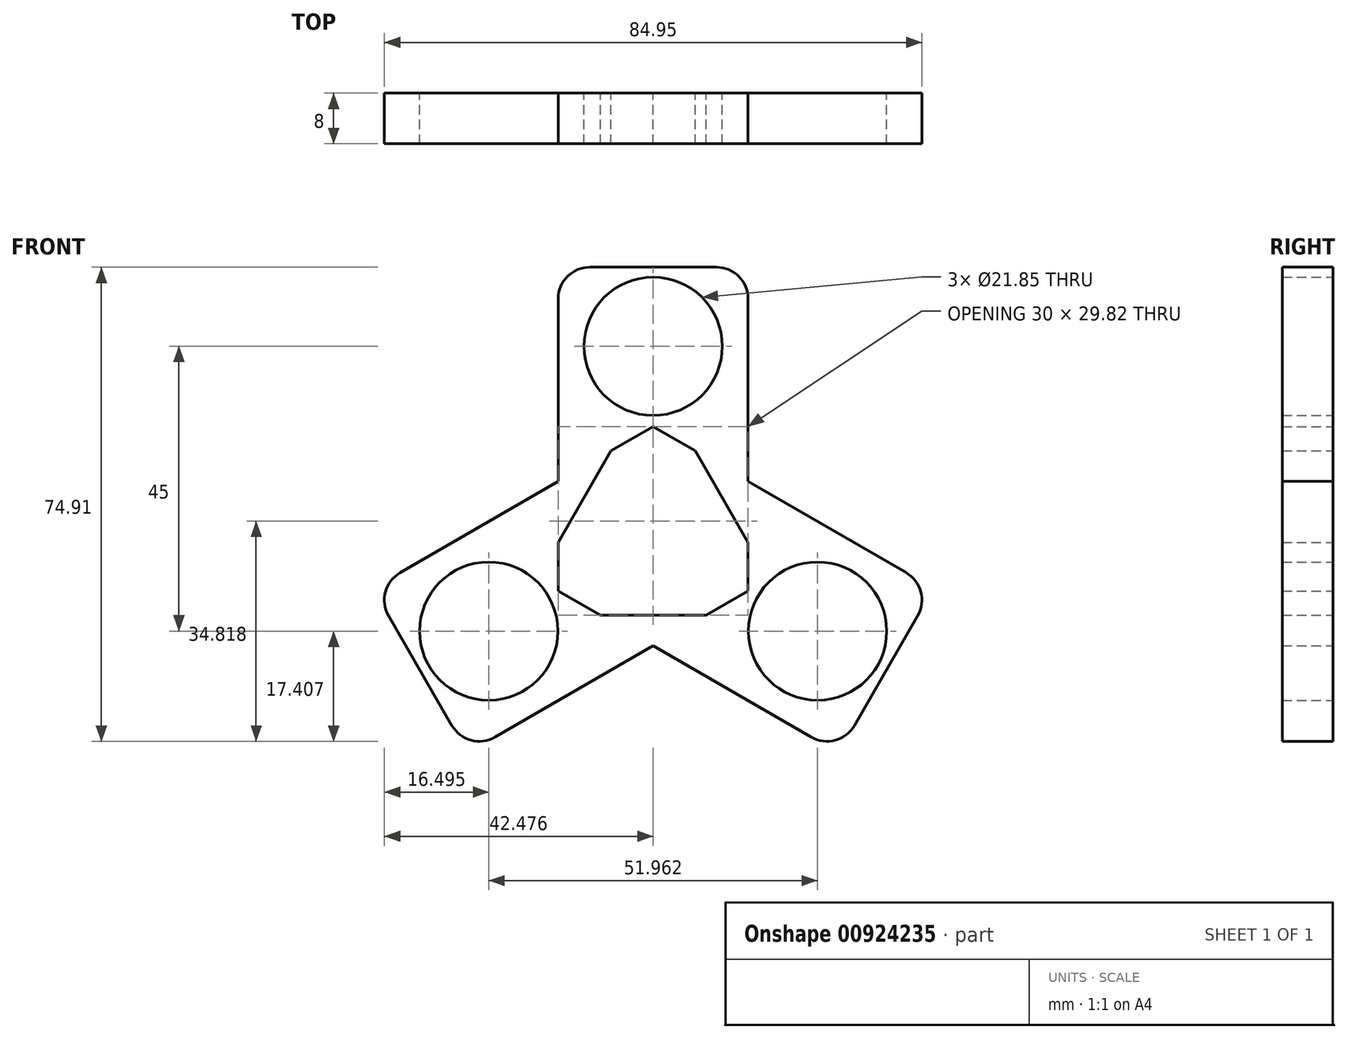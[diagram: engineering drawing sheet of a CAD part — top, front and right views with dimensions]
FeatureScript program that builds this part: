
annotation { "Feature Type Name" : "Feature", "Feature Type Description" : "" }
export const myFeature = defineFeature(function(context is Context, id is Id, definition is map)
    precondition{}
    {
        {
            var Q0;
            Q0=qCreatedBy(makeId("Front.planeOp"),FACE);
            var sketch = newSketch(context, id + "F0", { "sketchPlane" : qUnion([Q0])});
            skCircle(sketch, "E0", {"center": v(1107.53, 536.78) * mm, "radius": 10.93 * mm});
            skCircle(sketch, "E1", {"center": v(1107.53, 566.78) * mm, "radius": 10.93 * mm});
            skLineSegment(sketch, "E2", {"start": v(1107.53, 566.78) * mm, "end": v(1107.53, 536.78) * mm, "construction": true});
            skPoint(sketch, "E3", {"position": v(1107.53, 551.78) * mm});
            skLineSegment(sketch, "E4.bottom", {"start": v(1107.53, 551.78) * mm, "end": v(1107.53, 551.78) * mm});
            skLineSegment(sketch, "E4.top", {"start": v(1107.53, 554.4) * mm, "end": v(1107.53, 554.4) * mm});
            skLineSegment(sketch, "E4.left", {"start": v(1107.53, 551.78) * mm, "end": v(1107.53, 554.4) * mm});
            skLineSegment(sketch, "E4.right", {"start": v(1107.53, 551.78) * mm, "end": v(1107.53, 554.4) * mm});
            skPoint(sketch, "E4.middle", {"position": v(1107.53, 553.09) * mm});
            skLineSegment(sketch, "E5.bottom", {"start": v(1122.53, 524.28) * mm, "end": v(1092.53, 524.28) * mm});
            skLineSegment(sketch, "E5.top", {"start": v(1117.53, 579.28) * mm, "end": v(1097.53, 579.28) * mm});
            skLineSegment(sketch, "E5.left", {"start": v(1122.53, 524.28) * mm, "end": v(1122.53, 574.28) * mm});
            skLineSegment(sketch, "E5.right", {"start": v(1092.53, 524.28) * mm, "end": v(1092.53, 574.28) * mm});
            skPoint(sketch, "E6.visualSharp", {"position": v(1092.53, 579.28) * mm});
            skArc(sketch, "E6.filletArc", {"start": v(1097.53, 579.28) * mm, "mid": v(1093.99, 577.81) * mm, "end": v(1092.53, 574.28) * mm});
            skPoint(sketch, "E7.visualSharp", {"position": v(1122.53, 579.28) * mm});
            skArc(sketch, "E7.filletArc", {"start": v(1122.53, 574.28) * mm, "mid": v(1121.06, 577.81) * mm, "end": v(1117.53, 579.28) * mm});
            skLineSegment(sketch, "E8.1.0", {"start": v(1081.54, 521.78) * mm, "end": v(1107.53, 536.78) * mm, "construction": true});
            skCircle(sketch, "E8.1.1", {"center": v(1081.54, 521.78) * mm, "radius": 10.93 * mm});
            skLineSegment(sketch, "E8.1.2", {"start": v(1065.72, 524.19) * mm, "end": v(1075.72, 506.87) * mm});
            skLineSegment(sketch, "E8.1.3", {"start": v(1110.85, 556.02) * mm, "end": v(1125.85, 530.04) * mm});
            skLineSegment(sketch, "E8.1.5", {"start": v(1125.85, 530.04) * mm, "end": v(1082.55, 505.04) * mm});
            skLineSegment(sketch, "E8.1.6", {"start": v(1110.85, 556.02) * mm, "end": v(1067.55, 531.02) * mm});
            skPoint(sketch, "E8.1.7", {"position": v(1078.22, 502.54) * mm});
            skPoint(sketch, "E8.1.8", {"position": v(1063.22, 528.52) * mm});
            skPoint(sketch, "E8.1.9", {"position": v(1094.54, 529.28) * mm});
            skArc(sketch, "E8.1.10", {"start": v(1075.72, 506.87) * mm, "mid": v(1078.76, 504.54) * mm, "end": v(1082.55, 505.04) * mm});
            skPoint(sketch, "E8.1.11", {"position": v(1093.4, 528.62) * mm});
            skArc(sketch, "E8.1.12", {"start": v(1067.55, 531.02) * mm, "mid": v(1065.22, 527.98) * mm, "end": v(1065.72, 524.19) * mm});
            skPoint(sketch, "E8.1.13", {"position": v(1094.54, 529.28) * mm});
            skLineSegment(sketch, "E8.1.14", {"start": v(1094.54, 529.28) * mm, "end": v(1092.26, 527.97) * mm});
            skLineSegment(sketch, "E8.1.15", {"start": v(1094.54, 529.28) * mm, "end": v(1092.26, 527.97) * mm});
            skLineSegment(sketch, "E8.2.0", {"start": v(1133.5, 521.78) * mm, "end": v(1107.53, 536.78) * mm, "construction": true});
            skCircle(sketch, "E8.2.1", {"center": v(1133.5, 521.78) * mm, "radius": 10.93 * mm});
            skLineSegment(sketch, "E8.2.2", {"start": v(1139.33, 506.87) * mm, "end": v(1149.33, 524.19) * mm});
            skLineSegment(sketch, "E8.2.3", {"start": v(1089.2, 530.04) * mm, "end": v(1104.2, 556.02) * mm});
            skLineSegment(sketch, "E8.2.5", {"start": v(1104.2, 556.02) * mm, "end": v(1147.5, 531.02) * mm});
            skLineSegment(sketch, "E8.2.6", {"start": v(1089.2, 530.04) * mm, "end": v(1132.5, 505.04) * mm});
            skPoint(sketch, "E8.2.7", {"position": v(1151.83, 528.52) * mm});
            skPoint(sketch, "E8.2.8", {"position": v(1136.83, 502.54) * mm});
            skPoint(sketch, "E8.2.9", {"position": v(1120.52, 529.28) * mm});
            skArc(sketch, "E8.2.10", {"start": v(1149.33, 524.19) * mm, "mid": v(1149.83, 527.98) * mm, "end": v(1147.5, 531.02) * mm});
            skPoint(sketch, "E8.2.11", {"position": v(1121.65, 528.62) * mm});
            skArc(sketch, "E8.2.12", {"start": v(1132.5, 505.04) * mm, "mid": v(1136.3, 504.54) * mm, "end": v(1139.33, 506.87) * mm});
            skPoint(sketch, "E8.2.13", {"position": v(1120.52, 529.28) * mm});
            skLineSegment(sketch, "E8.2.14", {"start": v(1120.52, 529.28) * mm, "end": v(1122.79, 527.97) * mm});
            skLineSegment(sketch, "E8.2.15", {"start": v(1120.52, 529.28) * mm, "end": v(1122.79, 527.97) * mm});
            skSolve(sketch);
        }
        {
            var Q0;
            {var subQ0=sQuery(id+"F0.wireOp",EDGE,"E8.1.5");var subQ1=sQuery(id+"F0.wireOp",EDGE,"E5.bottom");var subQ2=makeQuery(id+"F0.imprint","INTERSECT",VERTEX,{"derivedFrom":[subQ1,subQ0]});Q0=makeQuery(id+"F0.imprint","IMPRINT",FACE,{"disambiguationData":[TD([[makeQuery(id+"F0.imprint","IMPRINT",EDGE,{"disambiguationData":[TD([[subQ2,-1.0]])],"derivedFrom":subQ1}),1.0]])]});}
            var Q1;
            {var subQ0=sQuery(id+"F0.wireOp",EDGE,"E8.2.5");var subQ1=sQuery(id+"F0.wireOp",EDGE,"E5.left");var subQ2=makeQuery(id+"F0.imprint","INTERSECT",VERTEX,{"derivedFrom":[subQ1,subQ0]});Q1=makeQuery(id+"F0.imprint","IMPRINT",FACE,{"disambiguationData":[TD([[makeQuery(id+"F0.imprint","IMPRINT",EDGE,{"disambiguationData":[TD([[subQ2,1.0]])],"derivedFrom":subQ1}),1.0]])]});}
            var Q2;
            {var subQ0=sQuery(id+"F0.wireOp",EDGE,"E8.1.6");var subQ1=sQuery(id+"F0.wireOp",EDGE,"E5.right");var subQ2=makeQuery(id+"F0.imprint","INTERSECT",VERTEX,{"derivedFrom":[subQ1,subQ0]});Q2=makeQuery(id+"F0.imprint","IMPRINT",FACE,{"disambiguationData":[TD([[makeQuery(id+"F0.imprint","IMPRINT",EDGE,{"disambiguationData":[TD([[subQ2,1.0]])],"derivedFrom":subQ1}),-1.0]])]});}
            var Q3;
            Q3=makeQuery(id+"F0.imprint","IMPRINT",FACE,{"disambiguationData":[TD([[makeQuery(id+"F0.imprint","IMPRINT",EDGE,{"derivedFrom":sQuery(id+"F0.wireOp",EDGE,"E1")}),-1.0]])]});
            var Q4;
            Q4=makeQuery(id+"F0.imprint","IMPRINT",FACE,{"disambiguationData":[TD([[makeQuery(id+"F0.imprint","IMPRINT",EDGE,{"derivedFrom":sQuery(id+"F0.wireOp",EDGE,"E8.1.1")}),-1.0]])]});
            var Q5;
            Q5=makeQuery(id+"F0.imprint","IMPRINT",FACE,{"disambiguationData":[TD([[makeQuery(id+"F0.imprint","IMPRINT",EDGE,{"derivedFrom":sQuery(id+"F0.wireOp",EDGE,"E0")}),-1.0]])]});
            var Q6;
            {var subQ0=sQuery(id+"F0.wireOp",EDGE,"E8.2.5");var subQ1=sQuery(id+"F0.wireOp",EDGE,"E8.1.6");var subQ2=makeQuery(id+"F0.imprint","INTERSECT",VERTEX,{"derivedFrom":[subQ1,subQ0]});Q6=makeQuery(id+"F0.imprint","IMPRINT",FACE,{"disambiguationData":[TD([[makeQuery(id+"F0.imprint","IMPRINT",EDGE,{"disambiguationData":[TD([[subQ2,-1.0]])],"derivedFrom":subQ1}),-1.0]])]});}
            var Q7;
            {var subQ0=sQuery(id+"F0.wireOp",EDGE,"E8.1.6");var subQ1=sQuery(id+"F0.wireOp",EDGE,"E8.1.3");var subQ2=makeQuery(id+"F0.imprint","INTERSECT",VERTEX,{"derivedFrom":[subQ1,subQ0]});Q7=makeQuery(id+"F0.imprint","IMPRINT",FACE,{"disambiguationData":[TD([[makeQuery(id+"F0.imprint","IMPRINT",EDGE,{"disambiguationData":[TD([[subQ2,-1.0]])],"derivedFrom":subQ1}),-1.0]])]});}
            var Q8;
            {var subQ0=sQuery(id+"F0.wireOp",EDGE,"E5.left");var subQ1=sQuery(id+"F0.wireOp",EDGE,"E5.bottom");var subQ2=makeQuery(id+"F0.imprint","INTERSECT",VERTEX,{"derivedFrom":[subQ1,subQ0]});Q8=makeQuery(id+"F0.imprint","IMPRINT",FACE,{"disambiguationData":[TD([[makeQuery(id+"F0.imprint","IMPRINT",EDGE,{"disambiguationData":[TD([[subQ2,-1.0]])],"derivedFrom":subQ1}),-1.0]])]});}
            var Q9;
            {var subQ0=sQuery(id+"F0.wireOp",EDGE,"E8.2.6");var subQ1=sQuery(id+"F0.wireOp",EDGE,"E5.right");var subQ2=makeQuery(id+"F0.imprint","INTERSECT",VERTEX,{"derivedFrom":[subQ1,subQ0]});Q9=makeQuery(id+"F0.imprint","IMPRINT",FACE,{"disambiguationData":[TD([[makeQuery(id+"F0.imprint","IMPRINT",EDGE,{"disambiguationData":[TD([[subQ2,-1.0]])],"derivedFrom":subQ1}),1.0]])]});}
            var Q10;
            {var subQ0=sQuery(id+"F0.wireOp",EDGE,"E5.right");var subQ1=sQuery(id+"F0.wireOp",EDGE,"E5.bottom");var subQ2=makeQuery(id+"F0.imprint","INTERSECT",VERTEX,{"derivedFrom":[subQ1,subQ0]});Q10=makeQuery(id+"F0.imprint","IMPRINT",FACE,{"disambiguationData":[TD([[makeQuery(id+"F0.imprint","IMPRINT",EDGE,{"disambiguationData":[TD([[subQ2,1.0]])],"derivedFrom":subQ1}),-1.0]])]});}
            var Q11;
            Q11=makeQuery(id+"F0.imprint","IMPRINT",FACE,{"disambiguationData":[TD([[makeQuery(id+"F0.imprint","IMPRINT",EDGE,{"derivedFrom":sQuery(id+"F0.wireOp",EDGE,"E8.2.1")}),-1.0]])]});
            var Q12;
            {var subQ0=sQuery(id+"F0.wireOp",EDGE,"E8.1.5");var subQ1=sQuery(id+"F0.wireOp",EDGE,"E5.left");var subQ2=makeQuery(id+"F0.imprint","INTERSECT",VERTEX,{"derivedFrom":[subQ1,subQ0]});Q12=makeQuery(id+"F0.imprint","IMPRINT",FACE,{"disambiguationData":[TD([[makeQuery(id+"F0.imprint","IMPRINT",EDGE,{"disambiguationData":[TD([[subQ2,-1.0]])],"derivedFrom":subQ1}),-1.0]])]});}
            extrude(context, id + "F1", {"entities" : qUnion([Q0, Q1, Q2, Q3, Q4, Q5, Q6, Q7, Q8, Q9, Q10, Q11, Q12]), "depth" : 8 * mm, "offsetDistance" : 25 * mm});
        }
    });
